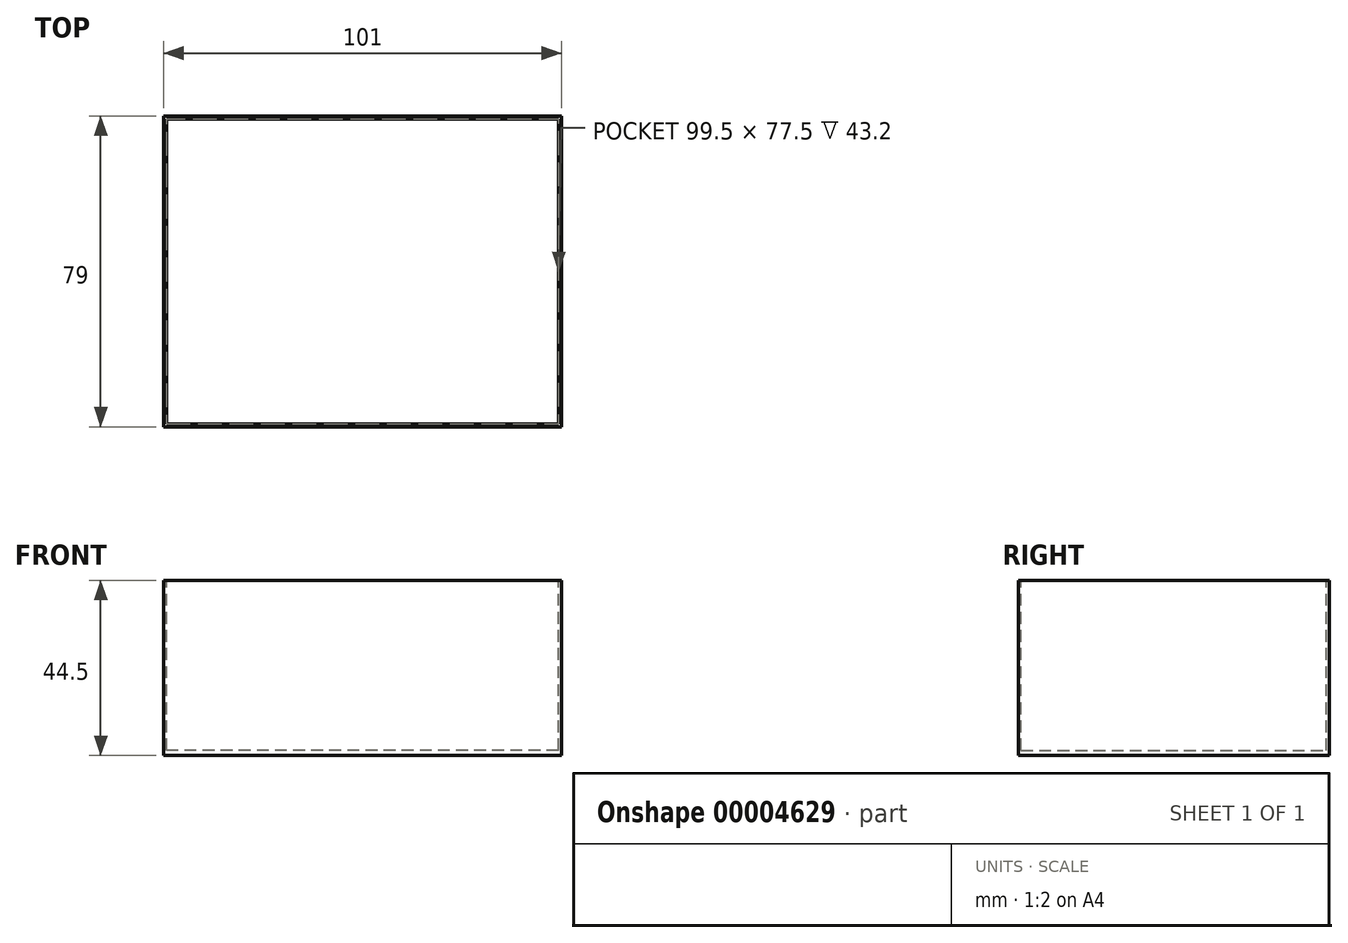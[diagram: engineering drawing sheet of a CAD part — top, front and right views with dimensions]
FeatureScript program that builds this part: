
annotation { "Feature Type Name" : "Feature", "Feature Type Description" : "" }
export const myFeature = defineFeature(function(context is Context, id is Id, definition is map)
    precondition{}
    {
        {
            var Q0;
            Q0=qCreatedBy(makeId("Top.planeOp"),FACE);
            var sketch = newSketch(context, id + "F0", { "sketchPlane" : qUnion([Q0])});
            skLineSegment(sketch, "E0.rect.bottom", {"start": v(50.5, -39.5) * mm, "end": v(-50.5, -39.5) * mm});
            skLineSegment(sketch, "E0.rect.top", {"start": v(50.5, 39.5) * mm, "end": v(-50.5, 39.5) * mm});
            skLineSegment(sketch, "E0.rect.left", {"start": v(50.5, -39.5) * mm, "end": v(50.5, 39.5) * mm});
            skLineSegment(sketch, "E0.rect.right", {"start": v(-50.5, -39.5) * mm, "end": v(-50.5, 39.5) * mm});
            skPoint(sketch, "E0.rect.middle", {"position": v(0, 0) * mm});
            skSolve(sketch);
        }
        {
            var Q0;
            Q0 = qSketchRegion(id + "F0", true);
            extrude(context, id + "F1", {"entities" : qUnion([Q0]), "depth" : 44.5 * mm});
        }
        {
            var Q0;
            Q0=makeQuery(id+"F1.opExtrude","CAP_FACE",FACE,{"disambiguationData":[OSD([sQuery(id+"F0.wireOp",EDGE,"E0.rect.bottom"),sQuery(id+"F0.wireOp",EDGE,"E0.rect.top"),sQuery(id+"F0.wireOp",EDGE,"E0.rect.left"),sQuery(id+"F0.wireOp",EDGE,"E0.rect.right")])],"isStart":false});
            var sketch = newSketch(context, id + "F2", { "sketchPlane" : qUnion([Q0])});
            skLineSegment(sketch, "E1.rect.bottom", {"start": v(49.75, -38.75) * mm, "end": v(-49.75, -38.75) * mm});
            skLineSegment(sketch, "E1.rect.top", {"start": v(49.75, 38.75) * mm, "end": v(-49.75, 38.75) * mm});
            skLineSegment(sketch, "E1.rect.left", {"start": v(49.75, -38.75) * mm, "end": v(49.75, 38.75) * mm});
            skLineSegment(sketch, "E1.rect.right", {"start": v(-49.75, -38.75) * mm, "end": v(-49.75, 38.75) * mm});
            skPoint(sketch, "E1.rect.middle", {"position": v(0, 0) * mm});
            skSolve(sketch);
        }
        {
            var Q0;
            Q0 = qSketchRegion(id + "F2", true);
            extrude(context, id + "F3", {"entities" : qUnion([Q0]), "operationType" : NewBodyOperationType.REMOVE, "oppositeDirection" : true, "depth" : 43.2 * mm});
        }
    });
